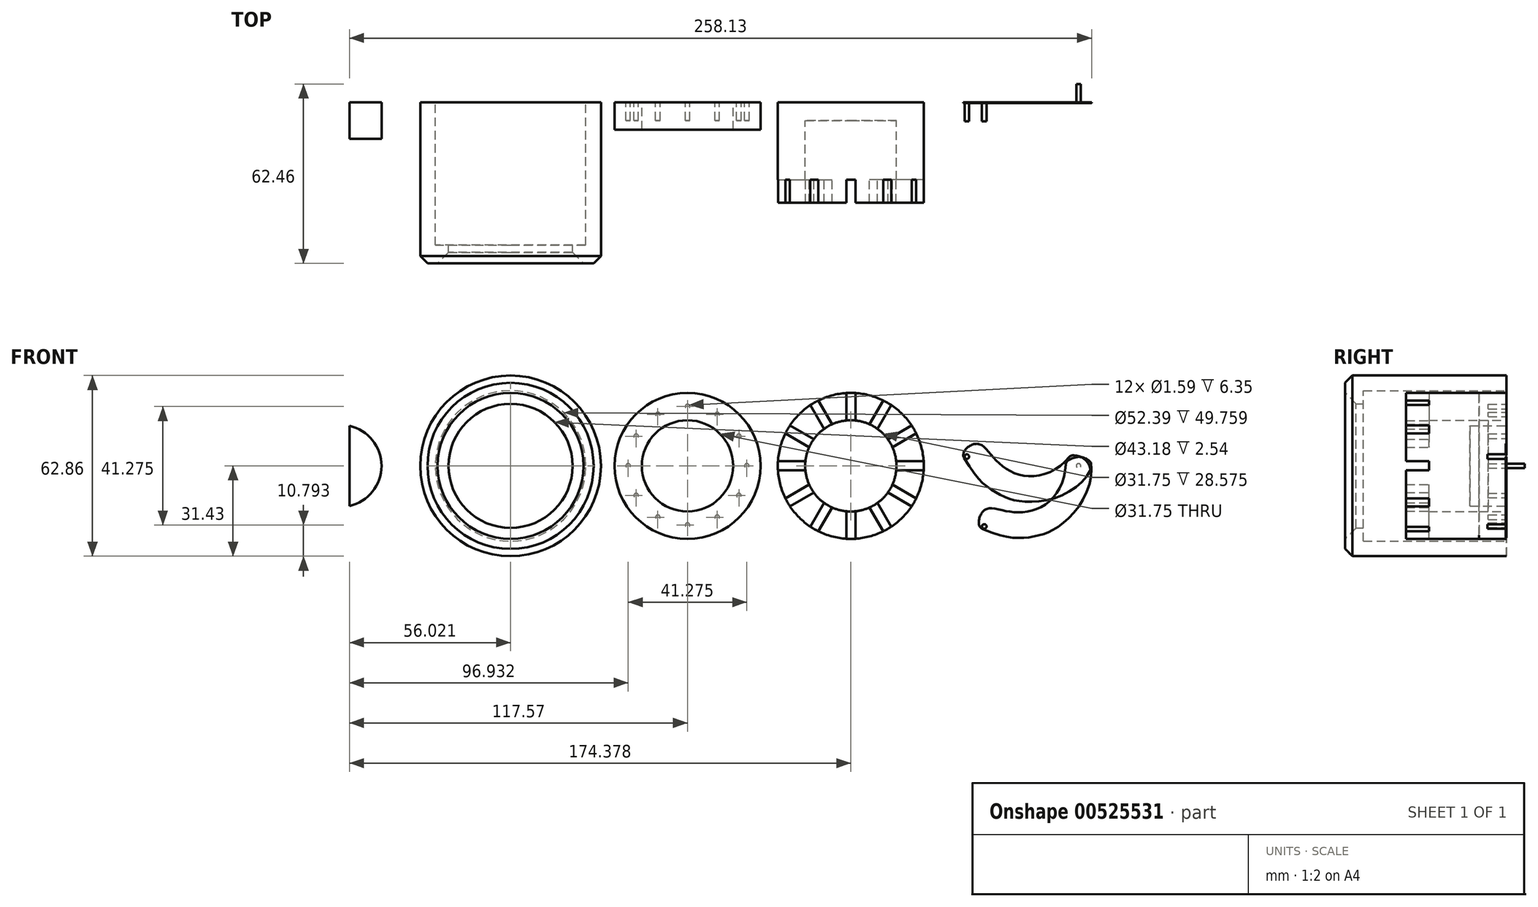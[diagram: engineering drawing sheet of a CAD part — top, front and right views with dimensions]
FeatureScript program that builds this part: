
annotation { "Feature Type Name" : "Feature", "Feature Type Description" : "" }
export const myFeature = defineFeature(function(context is Context, id is Id, definition is map)
    precondition{}
    {
        {
            var Q0;
            Q0=qCreatedBy(makeId("Front.planeOp"),FACE);
            var sketch = newSketch(context, id + "F0", { "sketchPlane" : qUnion([Q0])});
            skCircle(sketch, "E0", {"center": v(0, 0) * mm, "radius": 25.4 * mm});
            skCircle(sketch, "E1", {"center": v(0, 0) * mm, "radius": 15.88 * mm});
            skPoint(sketch, "E2", {"position": v(56.8, 0) * mm});
            skCircle(sketch, "E3", {"center": v(56.8, 0) * mm, "radius": 25.4 * mm});
            skCircle(sketch, "E4", {"center": v(56.8, 0) * mm, "radius": 15.88 * mm});
            skLineSegment(sketch, "E5", {"start": v(55.22, 25.35) * mm, "end": v(55.22, 15.8) * mm});
            skLineSegment(sketch, "E6", {"start": v(58.4, 25.35) * mm, "end": v(58.4, 15.8) * mm});
            skLineSegment(sketch, "E7", {"start": v(56.8, 0) * mm, "end": v(56.8, 25.4) * mm, "construction": true});
            skLineSegment(sketch, "E8", {"start": v(0, 0) * mm, "end": v(0, -25.4) * mm, "construction": true});
            skLineSegment(sketch, "E9", {"start": v(0, 0) * mm, "end": v(-25.4, 0) * mm, "construction": true});
            skLineSegment(sketch, "E10", {"start": v(0, 0) * mm, "end": v(-12.7, -22) * mm, "construction": true});
            skLineSegment(sketch, "E11", {"start": v(0, 0) * mm, "end": v(-22, -12.7) * mm, "construction": true});
            skCircle(sketch, "E12", {"center": v(0, 0) * mm, "radius": 20.64 * mm, "construction": true});
            skPoint(sketch, "E13.MirrorP", {"position": v(0, -20.64) * mm});
            skLineSegment(sketch, "E14", {"start": v(56.8, 0) * mm, "end": v(31.4, 0) * mm, "construction": true});
            skLineSegment(sketch, "E15", {"start": v(56.8, 0) * mm, "end": v(44.1, 22) * mm, "construction": true});
            skLineSegment(sketch, "E16", {"start": v(56.8, 0) * mm, "end": v(34.81, 12.7) * mm, "construction": true});
            skCircle(sketch, "E17", {"center": v(0, -20.64) * mm, "radius": 0.8 * mm});
            skPoint(sketch, "E18", {"position": v(115.4, 0) * mm});
            skCircle(sketch, "E19", {"center": v(115.4, 0) * mm, "radius": 15.88 * mm});
            skCircle(sketch, "E20", {"center": v(115.4, 0) * mm, "radius": 25.4 * mm});
            skLineSegment(sketch, "E21", {"start": v(115.4, 0) * mm, "end": v(140.8, 0) * mm, "construction": true});
            skLineSegment(sketch, "E22", {"start": v(115.4, 0) * mm, "end": v(115.4, -25.4) * mm, "construction": true});
            skLineSegment(sketch, "E23", {"start": v(115.4, 0) * mm, "end": v(137.4, -12.7) * mm, "construction": true});
            skLineSegment(sketch, "E24", {"start": v(115.4, 0) * mm, "end": v(128.1, -22) * mm, "construction": true});
            skLineSegment(sketch, "E25", {"start": v(115.4, 0) * mm, "end": v(102.7, -22) * mm, "construction": true});
            skCircle(sketch, "E26", {"center": v(115.4, 0) * mm, "radius": 20.64 * mm, "construction": true});
            skPoint(sketch, "E27", {"position": v(136.04, 0) * mm});
            skCircle(sketch, "E28", {"center": v(136.04, 0) * mm, "radius": 0.8 * mm});
            skPoint(sketch, "E29", {"position": v(103.23, -21.08) * mm});
            skCircle(sketch, "E30", {"center": v(103.23, -21.08) * mm, "radius": 0.8 * mm});
            skLineSegment(sketch, "E31", {"start": v(103.23, -21.08) * mm, "end": v(102.7, -22) * mm, "construction": true});
            skCircle(sketch, "E32.1.0", {"center": v(-10.32, -17.87) * mm, "radius": 0.8 * mm});
            skCircle(sketch, "E32.2.0", {"center": v(-17.87, -10.32) * mm, "radius": 0.8 * mm});
            skCircle(sketch, "E32.3.0", {"center": v(-20.64, 0) * mm, "radius": 0.8 * mm});
            skCircle(sketch, "E32.4.0", {"center": v(-17.87, 10.32) * mm, "radius": 0.8 * mm});
            skCircle(sketch, "E32.5.0", {"center": v(-10.32, 17.87) * mm, "radius": 0.8 * mm});
            skCircle(sketch, "E32.6.0", {"center": v(0, 20.64) * mm, "radius": 0.8 * mm});
            skCircle(sketch, "E32.7.0", {"center": v(10.32, 17.87) * mm, "radius": 0.8 * mm});
            skCircle(sketch, "E32.8.0", {"center": v(17.87, 10.32) * mm, "radius": 0.8 * mm});
            skCircle(sketch, "E32.9.0", {"center": v(20.64, 0) * mm, "radius": 0.8 * mm});
            skCircle(sketch, "E32.10.0", {"center": v(17.87, -10.32) * mm, "radius": 0.8 * mm});
            skCircle(sketch, "E32.11.0", {"center": v(10.32, -17.87) * mm, "radius": 0.8 * mm});
            skLineSegment(sketch, "E32.anchor1", {"start": v(0, 0) * mm, "end": v(0, -20.64) * mm, "construction": true});
            skLineSegment(sketch, "E32.anchor2", {"start": v(0, 0) * mm, "end": v(10.32, -17.87) * mm, "construction": true});
            skLineSegment(sketch, "E33.1.0", {"start": v(68.1, 22.75) * mm, "end": v(63.33, 14.47) * mm});
            skLineSegment(sketch, "E33.1.1", {"start": v(70.86, 21.16) * mm, "end": v(66.08, 12.89) * mm});
            skLineSegment(sketch, "E33.2.0", {"start": v(77.97, 14.05) * mm, "end": v(69.7, 9.27) * mm});
            skLineSegment(sketch, "E33.2.1", {"start": v(79.56, 11.3) * mm, "end": v(71.28, 6.52) * mm});
            skLineSegment(sketch, "E33.3.0", {"start": v(82.16, 1.59) * mm, "end": v(72.6, 1.59) * mm});
            skLineSegment(sketch, "E33.3.1", {"start": v(82.16, -1.59) * mm, "end": v(72.6, -1.59) * mm});
            skLineSegment(sketch, "E33.4.0", {"start": v(79.56, -11.3) * mm, "end": v(71.28, -6.52) * mm});
            skLineSegment(sketch, "E33.4.1", {"start": v(77.97, -14.05) * mm, "end": v(69.7, -9.27) * mm});
            skLineSegment(sketch, "E33.5.0", {"start": v(70.86, -21.16) * mm, "end": v(66.08, -12.89) * mm});
            skLineSegment(sketch, "E33.5.1", {"start": v(68.1, -22.75) * mm, "end": v(63.33, -14.47) * mm});
            skLineSegment(sketch, "E33.6.0", {"start": v(58.4, -25.35) * mm, "end": v(58.4, -15.8) * mm});
            skLineSegment(sketch, "E33.6.1", {"start": v(55.22, -25.35) * mm, "end": v(55.22, -15.8) * mm});
            skLineSegment(sketch, "E33.7.0", {"start": v(45.5, -22.75) * mm, "end": v(50.29, -14.47) * mm});
            skLineSegment(sketch, "E33.7.1", {"start": v(42.76, -21.16) * mm, "end": v(47.54, -12.89) * mm});
            skLineSegment(sketch, "E33.8.0", {"start": v(35.65, -14.05) * mm, "end": v(43.92, -9.27) * mm});
            skLineSegment(sketch, "E33.8.1", {"start": v(34.06, -11.3) * mm, "end": v(42.34, -6.52) * mm});
            skLineSegment(sketch, "E33.9.0", {"start": v(31.46, -1.59) * mm, "end": v(41.01, -1.59) * mm});
            skLineSegment(sketch, "E33.9.1", {"start": v(31.46, 1.59) * mm, "end": v(41.01, 1.59) * mm});
            skLineSegment(sketch, "E33.10.0", {"start": v(34.06, 11.3) * mm, "end": v(42.34, 6.52) * mm});
            skLineSegment(sketch, "E33.10.1", {"start": v(35.65, 14.05) * mm, "end": v(43.92, 9.27) * mm});
            skLineSegment(sketch, "E33.11.0", {"start": v(42.76, 21.16) * mm, "end": v(47.54, 12.89) * mm});
            skLineSegment(sketch, "E33.11.1", {"start": v(45.5, 22.75) * mm, "end": v(50.29, 14.47) * mm});
            skLineSegment(sketch, "E33.anchor1", {"start": v(56.8, 0) * mm, "end": v(55.22, 15.8) * mm, "construction": true});
            skLineSegment(sketch, "E33.anchor2", {"start": v(56.8, 0) * mm, "end": v(47.54, 12.89) * mm, "construction": true});
            skFitSpline(sketch, "E34", {"points": [v(104.11, -15.02) * mm, v(107.92, -15.1) * mm, v(115.4, -16.16) * mm, v(125.15, -12.93) * mm, v(131.55, 0.54) * mm], "startDerivative": vector(16.12, 9.46) * mm, "endDerivative": vector(0.3, 52.9) * mm});
            skFitSpline(sketch, "E35", {"points": [v(140.3, 1) * mm, v(137.15, -12.55) * mm, v(127.97, -21.77) * mm, v(121.95, -24.26) * mm, v(115.4, -25.08) * mm, v(102.7, -22) * mm], "startDerivative": vector(11.31, -46.24) * mm, "endDerivative": vector(-81.58, 33.81) * mm});
            skFitSpline(sketch, "E36", {"points": [v(140.3, 1) * mm, v(135.8, 3.1) * mm, v(131.55, 0.54) * mm], "startDerivative": vector(-1.34, 5.76) * mm, "endDerivative": vector(0.7, -5.07) * mm});
            skFitSpline(sketch, "E37", {"points": [v(104.11, -15.02) * mm, v(102.7, -22) * mm], "startDerivative": vector(-6.78, -1.61) * mm, "endDerivative": vector(8.29, -3.99) * mm});
            skPoint(sketch, "E38", {"position": v(-61.55, 0) * mm});
            skCircle(sketch, "E39", {"center": v(-61.55, 0) * mm, "radius": 25.4 * mm, "construction": true});
            skLineSegment(sketch, "E40", {"start": v(-61.55, 25.4) * mm, "end": v(-61.55, 26.2) * mm, "construction": true});
            skCircle(sketch, "E41", {"center": v(-61.55, 0) * mm, "radius": 26.2 * mm});
            skLineSegment(sketch, "E42", {"start": v(-61.55, 26.2) * mm, "end": v(-61.55, 31.43) * mm, "construction": true});
            skCircle(sketch, "E43", {"center": v(-61.55, 0) * mm, "radius": 31.43 * mm});
            skPoint(sketch, "E44", {"position": v(-120.75, 0) * mm});
            skCircle(sketch, "E45", {"center": v(-120.75, 0) * mm, "radius": 15.88 * mm, "construction": true});
            skLineSegment(sketch, "E46", {"start": v(-120.75, 14.29) * mm, "end": v(-120.75, 15.88) * mm, "construction": true});
            skCircle(sketch, "E47", {"center": v(-120.75, 0) * mm, "radius": 14.29 * mm});
            skLineSegment(sketch, "E48", {"start": v(-120.75, 14.29) * mm, "end": v(-120.75, -14.29) * mm, "construction": true});
            skLineSegment(sketch, "E49", {"start": v(-117.57, 13.93) * mm, "end": v(-117.57, -13.93) * mm});
            skLineSegment(sketch, "E50", {"start": v(-120.75, 0) * mm, "end": v(-117.57, 0) * mm, "construction": true});
            skCircle(sketch, "E51", {"center": v(-61.55, 0) * mm, "radius": 15.88 * mm, "construction": true});
            skLineSegment(sketch, "E52", {"start": v(-61.55, 25.4) * mm, "end": v(-61.55, 15.88) * mm, "construction": true});
            skCircle(sketch, "E53", {"center": v(-61.55, 0) * mm, "radius": 21.6 * mm});
            skLineSegment(sketch, "E54", {"start": v(-83.14, 0) * mm, "end": v(-86.95, 0) * mm, "construction": true});
            skSolve(sketch);
        }
        {
            var Q0;
            Q0=makeQuery(id+"F0.imprint","IMPRINT",FACE,{"disambiguationData":[TD([[makeQuery(id+"F0.imprint","IMPRINT",EDGE,{"derivedFrom":sQuery(id+"F0.wireOp",EDGE,"E0")}),1.0]])]});
            extrude(context, id + "F1", {"entities" : qUnion([Q0]), "depth" : 9.52 * mm, "offsetDistance" : 25.4 * mm});
        }
        {
            var Q0;
            Q0=makeQuery(id+"F0.imprint","IMPRINT",FACE,{"disambiguationData":[TD([[makeQuery(id+"F0.imprint","IMPRINT",EDGE,{"derivedFrom":sQuery(id+"F0.wireOp",EDGE,"s6iMMyBa-D8Xy-xpaJ-yUIR-B6XonEqi0sU5")}),1.0]])]});
            var Q1;
            Q1=makeQuery(id+"F0.imprint","IMPRINT",FACE,{"disambiguationData":[TD([[makeQuery(id+"F0.imprint","IMPRINT",EDGE,{"derivedFrom":sQuery(id+"F0.wireOp",EDGE,"E17")}),1.0]])]});
            var Q2;
            Q2=makeQuery(id+"F0.imprint","IMPRINT",FACE,{"disambiguationData":[TD([[makeQuery(id+"F0.imprint","IMPRINT",EDGE,{"derivedFrom":sQuery(id+"F0.wireOp",EDGE,"AtIlf3Au-Bq7Z-XsMa-0TNi-mlutI5QVi0Vg")}),1.0]])]});
            var Q3;
            Q3=makeQuery(id+"F0.imprint","IMPRINT",FACE,{"disambiguationData":[TD([[makeQuery(id+"F0.imprint","IMPRINT",EDGE,{"derivedFrom":sQuery(id+"F0.wireOp",EDGE,"LPBVN7vU-9lCU-ToEj-kHmf-HtTOnWTrnx0X")}),1.0]])]});
            var Q4;
            Q4=makeQuery(id+"F0.imprint","IMPRINT",FACE,{"disambiguationData":[TD([[makeQuery(id+"F0.imprint","IMPRINT",EDGE,{"derivedFrom":sQuery(id+"F0.wireOp",EDGE,"7G2NKrnm-SsA4-xEUf-SBrS-4CvmUcFiUhnw")}),1.0]])]});
            var Q5;
            Q5=makeQuery(id+"F0.imprint","IMPRINT",FACE,{"disambiguationData":[TD([[makeQuery(id+"F0.imprint","IMPRINT",EDGE,{"derivedFrom":sQuery(id+"F0.wireOp",EDGE,"5kcASDks-mq9c-bl9G-Ueh7-qEfE6t67Ye5v")}),1.0]])]});
            var Q6;
            Q6=makeQuery(id+"F0.imprint","IMPRINT",FACE,{"disambiguationData":[TD([[makeQuery(id+"F0.imprint","IMPRINT",EDGE,{"derivedFrom":sQuery(id+"F0.wireOp",EDGE,"E8oFIRYm-xzG7-Hb76-Ff9d-wAEOmmFZPbMu")}),1.0]])]});
            var Q7;
            Q7=makeQuery(id+"F0.imprint","IMPRINT",FACE,{"disambiguationData":[TD([[makeQuery(id+"F0.imprint","IMPRINT",EDGE,{"derivedFrom":sQuery(id+"F0.wireOp",EDGE,"81BxfGTd-YKAY-64cZ-fL0K-wmXlntmFN0K0")}),1.0]])]});
            var Q8;
            Q8=makeQuery(id+"F0.imprint","IMPRINT",FACE,{"disambiguationData":[TD([[makeQuery(id+"F0.imprint","IMPRINT",EDGE,{"derivedFrom":sQuery(id+"F0.wireOp",EDGE,"69LZ1IFe-H8bj-blPN-723C-wDsHpG4YcniU")}),1.0]])]});
            var Q9;
            Q9=makeQuery(id+"F0.imprint","IMPRINT",FACE,{"disambiguationData":[TD([[makeQuery(id+"F0.imprint","IMPRINT",EDGE,{"derivedFrom":sQuery(id+"F0.wireOp",EDGE,"Z80VmrJO-JPsI-7q49-229l-mwXOrK1fiucL")}),1.0]])]});
            var Q10;
            Q10=makeQuery(id+"F0.imprint","IMPRINT",FACE,{"disambiguationData":[TD([[makeQuery(id+"F0.imprint","IMPRINT",EDGE,{"derivedFrom":sQuery(id+"F0.wireOp",EDGE,"RLDDLLrd-eygd-P5LT-ErYo-oTRXF8rHV5MU")}),1.0]])]});
            var Q11;
            Q11=makeQuery(id+"F0.imprint","IMPRINT",FACE,{"disambiguationData":[TD([[makeQuery(id+"F0.imprint","IMPRINT",EDGE,{"derivedFrom":sQuery(id+"F0.wireOp",EDGE,"8nB9dmYy-pceP-ION0-gW85-PYhLIlr7NmiF")}),1.0]])]});
            var Q12;
            Q12=makeQuery(id+"F0.imprint","IMPRINT",FACE,{"disambiguationData":[TD([[makeQuery(id+"F0.imprint","IMPRINT",EDGE,{"derivedFrom":sQuery(id+"F0.wireOp",EDGE,"E32.1.0")}),1.0]])]});
            var Q13;
            Q13=makeQuery(id+"F0.imprint","IMPRINT",FACE,{"disambiguationData":[TD([[makeQuery(id+"F0.imprint","IMPRINT",EDGE,{"derivedFrom":sQuery(id+"F0.wireOp",EDGE,"E32.2.0")}),1.0]])]});
            var Q14;
            Q14=makeQuery(id+"F0.imprint","IMPRINT",FACE,{"disambiguationData":[TD([[makeQuery(id+"F0.imprint","IMPRINT",EDGE,{"derivedFrom":sQuery(id+"F0.wireOp",EDGE,"E32.3.0")}),1.0]])]});
            var Q15;
            Q15=makeQuery(id+"F0.imprint","IMPRINT",FACE,{"disambiguationData":[TD([[makeQuery(id+"F0.imprint","IMPRINT",EDGE,{"derivedFrom":sQuery(id+"F0.wireOp",EDGE,"E32.4.0")}),1.0]])]});
            var Q16;
            Q16=makeQuery(id+"F0.imprint","IMPRINT",FACE,{"disambiguationData":[TD([[makeQuery(id+"F0.imprint","IMPRINT",EDGE,{"derivedFrom":sQuery(id+"F0.wireOp",EDGE,"E32.8.0")}),1.0]])]});
            var Q17;
            Q17=makeQuery(id+"F0.imprint","IMPRINT",FACE,{"disambiguationData":[TD([[makeQuery(id+"F0.imprint","IMPRINT",EDGE,{"derivedFrom":sQuery(id+"F0.wireOp",EDGE,"E32.9.0")}),1.0]])]});
            var Q18;
            Q18=makeQuery(id+"F0.imprint","IMPRINT",FACE,{"disambiguationData":[TD([[makeQuery(id+"F0.imprint","IMPRINT",EDGE,{"derivedFrom":sQuery(id+"F0.wireOp",EDGE,"E32.10.0")}),1.0]])]});
            var Q19;
            Q19=makeQuery(id+"F0.imprint","IMPRINT",FACE,{"disambiguationData":[TD([[makeQuery(id+"F0.imprint","IMPRINT",EDGE,{"derivedFrom":sQuery(id+"F0.wireOp",EDGE,"E32.11.0")}),1.0]])]});
            var Q20;
            Q20=makeQuery(id+"F0.imprint","IMPRINT",FACE,{"disambiguationData":[TD([[makeQuery(id+"F0.imprint","IMPRINT",EDGE,{"derivedFrom":sQuery(id+"F0.wireOp",EDGE,"E32.5.0")}),1.0]])]});
            var Q21;
            Q21=makeQuery(id+"F0.imprint","IMPRINT",FACE,{"disambiguationData":[TD([[makeQuery(id+"F0.imprint","IMPRINT",EDGE,{"derivedFrom":sQuery(id+"F0.wireOp",EDGE,"E32.6.0")}),1.0]])]});
            var Q22;
            Q22=makeQuery(id+"F0.imprint","IMPRINT",FACE,{"disambiguationData":[TD([[makeQuery(id+"F0.imprint","IMPRINT",EDGE,{"derivedFrom":sQuery(id+"F0.wireOp",EDGE,"E32.7.0")}),1.0]])]});
            extrude(context, id + "F2", {"entities" : qUnion([Q0, Q1, Q2, Q3, Q4, Q5, Q6, Q7, Q8, Q9, Q10, Q11, Q12, Q13, Q14, Q15, Q16, Q17, Q18, Q19, Q20, Q21, Q22]), "operationType" : NewBodyOperationType.ADD, "depth" : 9.52 * mm, "offsetDistance" : 25.4 * mm, "hasSecondDirection" : true, "secondDirectionOppositeDirection" : false, "secondDirectionDepth" : 6.35 * mm});
        }
        {
            var Q0;
            {var subQ0=sQuery(id+"F0.wireOp",EDGE,"E5");Q0=makeQuery(id+"F0.imprint","IMPRINT",FACE,{"disambiguationData":[TD([[makeQuery(id+"F0.imprint","IMPRINT",EDGE,{"derivedFrom":subQ0}),-1.0]])]});}
            var Q1;
            {var subQ0=sQuery(id+"F0.wireOp",EDGE,"E6");Q1=makeQuery(id+"F0.imprint","IMPRINT",FACE,{"disambiguationData":[TD([[makeQuery(id+"F0.imprint","IMPRINT",EDGE,{"derivedFrom":subQ0}),1.0]])]});}
            var Q2;
            {var subQ0=sQuery(id+"F0.wireOp",EDGE,"fbf749ff-cb35-4a6c-9a33-f2034c6c4bd01.MirrorCS");Q2=makeQuery(id+"F0.imprint","IMPRINT",FACE,{"disambiguationData":[TD([[makeQuery(id+"F0.imprint","IMPRINT",EDGE,{"derivedFrom":subQ0}),-1.0]])]});}
            var Q3;
            {var subQ0=sQuery(id+"F0.wireOp",EDGE,"2fd75d67-c833-453d-aed9-928d4629f6e80.MirrorCS");Q3=makeQuery(id+"F0.imprint","IMPRINT",FACE,{"disambiguationData":[TD([[makeQuery(id+"F0.imprint","IMPRINT",EDGE,{"derivedFrom":subQ0}),1.0]])]});}
            var Q4;
            {var subQ0=sQuery(id+"F0.wireOp",EDGE,"2fd75d67-c833-453d-aed9-928d4629f6e81.MirrorCS");Q4=makeQuery(id+"F0.imprint","IMPRINT",FACE,{"disambiguationData":[TD([[makeQuery(id+"F0.imprint","IMPRINT",EDGE,{"derivedFrom":subQ0}),-1.0]])]});}
            var Q5;
            {var subQ0=sQuery(id+"F0.wireOp",EDGE,"f250c77a-9c41-4284-acdc-d1beea1743cd4.MirrorCS");Q5=makeQuery(id+"F0.imprint","IMPRINT",FACE,{"disambiguationData":[TD([[makeQuery(id+"F0.imprint","IMPRINT",EDGE,{"derivedFrom":subQ0}),-1.0]])]});}
            var Q6;
            {var subQ0=sQuery(id+"F0.wireOp",EDGE,"0f70c7a6-16d2-4b7e-8e74-36adbd6650231.MirrorCS");Q6=makeQuery(id+"F0.imprint","IMPRINT",FACE,{"disambiguationData":[TD([[makeQuery(id+"F0.imprint","IMPRINT",EDGE,{"derivedFrom":subQ0}),-1.0]])]});}
            var Q7;
            {var subQ0=sQuery(id+"F0.wireOp",EDGE,"0f70c7a6-16d2-4b7e-8e74-36adbd6650230.MirrorCS");Q7=makeQuery(id+"F0.imprint","IMPRINT",FACE,{"disambiguationData":[TD([[makeQuery(id+"F0.imprint","IMPRINT",EDGE,{"derivedFrom":subQ0}),1.0]])]});}
            var Q8;
            {var subQ0=sQuery(id+"F0.wireOp",EDGE,"f250c77a-9c41-4284-acdc-d1beea1743cd1.MirrorCS");Q8=makeQuery(id+"F0.imprint","IMPRINT",FACE,{"disambiguationData":[TD([[makeQuery(id+"F0.imprint","IMPRINT",EDGE,{"derivedFrom":subQ0}),1.0]])]});}
            var Q9;
            {var subQ0=sQuery(id+"F0.wireOp",EDGE,"9w2d8wIe-WXym-CVrp-cu3j-IBF0zttnJeDN");Q9=makeQuery(id+"F0.imprint","IMPRINT",FACE,{"disambiguationData":[TD([[makeQuery(id+"F0.imprint","IMPRINT",EDGE,{"derivedFrom":subQ0}),1.0]])]});}
            var Q10;
            {var subQ0=sQuery(id+"F0.wireOp",EDGE,"rNfeRRnT-j6xk-gXZh-7wYH-FjU2ABQCOJYs");Q10=makeQuery(id+"F0.imprint","IMPRINT",FACE,{"disambiguationData":[TD([[makeQuery(id+"F0.imprint","IMPRINT",EDGE,{"derivedFrom":subQ0}),-1.0]])]});}
            var Q11;
            {var subQ0=sQuery(id+"F0.wireOp",EDGE,"0O4XiFiV-CEn2-lq8x-aV4j-AC8LqMBIBljq");Q11=makeQuery(id+"F0.imprint","IMPRINT",FACE,{"disambiguationData":[TD([[makeQuery(id+"F0.imprint","IMPRINT",EDGE,{"derivedFrom":subQ0}),-1.0]])]});}
            var Q12;
            {var subQ0=sQuery(id+"F0.wireOp",EDGE,"E33.1.1");Q12=makeQuery(id+"F0.imprint","IMPRINT",FACE,{"disambiguationData":[TD([[makeQuery(id+"F0.imprint","IMPRINT",EDGE,{"derivedFrom":subQ0}),1.0]])]});}
            var Q13;
            {var subQ0=sQuery(id+"F0.wireOp",EDGE,"E33.10.1");Q13=makeQuery(id+"F0.imprint","IMPRINT",FACE,{"disambiguationData":[TD([[makeQuery(id+"F0.imprint","IMPRINT",EDGE,{"derivedFrom":subQ0}),1.0]])]});}
            var Q14;
            {var subQ0=sQuery(id+"F0.wireOp",EDGE,"E33.9.1");Q14=makeQuery(id+"F0.imprint","IMPRINT",FACE,{"disambiguationData":[TD([[makeQuery(id+"F0.imprint","IMPRINT",EDGE,{"derivedFrom":subQ0}),1.0]])]});}
            var Q15;
            {var subQ0=sQuery(id+"F0.wireOp",EDGE,"E33.8.1");Q15=makeQuery(id+"F0.imprint","IMPRINT",FACE,{"disambiguationData":[TD([[makeQuery(id+"F0.imprint","IMPRINT",EDGE,{"derivedFrom":subQ0}),1.0]])]});}
            var Q16;
            {var subQ0=sQuery(id+"F0.wireOp",EDGE,"E33.7.1");Q16=makeQuery(id+"F0.imprint","IMPRINT",FACE,{"disambiguationData":[TD([[makeQuery(id+"F0.imprint","IMPRINT",EDGE,{"derivedFrom":subQ0}),1.0]])]});}
            var Q17;
            {var subQ0=sQuery(id+"F0.wireOp",EDGE,"E33.6.1");Q17=makeQuery(id+"F0.imprint","IMPRINT",FACE,{"disambiguationData":[TD([[makeQuery(id+"F0.imprint","IMPRINT",EDGE,{"derivedFrom":subQ0}),1.0]])]});}
            var Q18;
            {var subQ0=sQuery(id+"F0.wireOp",EDGE,"E33.5.1");Q18=makeQuery(id+"F0.imprint","IMPRINT",FACE,{"disambiguationData":[TD([[makeQuery(id+"F0.imprint","IMPRINT",EDGE,{"derivedFrom":subQ0}),1.0]])]});}
            var Q19;
            {var subQ0=sQuery(id+"F0.wireOp",EDGE,"E33.4.1");Q19=makeQuery(id+"F0.imprint","IMPRINT",FACE,{"disambiguationData":[TD([[makeQuery(id+"F0.imprint","IMPRINT",EDGE,{"derivedFrom":subQ0}),1.0]])]});}
            var Q20;
            {var subQ0=sQuery(id+"F0.wireOp",EDGE,"E33.3.1");Q20=makeQuery(id+"F0.imprint","IMPRINT",FACE,{"disambiguationData":[TD([[makeQuery(id+"F0.imprint","IMPRINT",EDGE,{"derivedFrom":subQ0}),1.0]])]});}
            var Q21;
            {var subQ0=sQuery(id+"F0.wireOp",EDGE,"E33.2.1");Q21=makeQuery(id+"F0.imprint","IMPRINT",FACE,{"disambiguationData":[TD([[makeQuery(id+"F0.imprint","IMPRINT",EDGE,{"derivedFrom":subQ0}),1.0]])]});}
            extrude(context, id + "F3", {"entities" : qUnion([Q0, Q1, Q2, Q3, Q4, Q5, Q6, Q7, Q8, Q9, Q10, Q11, Q12, Q13, Q14, Q15, Q16, Q17, Q18, Q19, Q20, Q21]), "depth" : 34.92 * mm, "offsetDistance" : 25.4 * mm});
        }
        {
            var Q0;
            {var subQ0=sQuery(id+"F0.wireOp",EDGE,"ZaU0kOoB-QJxD-Patt-xqo6-pcWAK5y8749o");Q0=makeQuery(id+"F0.imprint","IMPRINT",FACE,{"disambiguationData":[TD([[makeQuery(id+"F0.imprint","IMPRINT",EDGE,{"derivedFrom":subQ0}),1.0]])]});}
            var Q1;
            {var subQ0=sQuery(id+"F0.wireOp",EDGE,"wwbT7rCj-GxeO-RORG-loiN-BMqO9dk52bbs");Q1=makeQuery(id+"F0.imprint","IMPRINT",FACE,{"disambiguationData":[TD([[makeQuery(id+"F0.imprint","IMPRINT",EDGE,{"derivedFrom":subQ0}),1.0]])]});}
            var Q2;
            {var subQ0=sQuery(id+"F0.wireOp",EDGE,"rNfeRRnT-j6xk-gXZh-7wYH-FjU2ABQCOJYs");Q2=makeQuery(id+"F0.imprint","IMPRINT",FACE,{"disambiguationData":[TD([[makeQuery(id+"F0.imprint","IMPRINT",EDGE,{"derivedFrom":subQ0}),1.0]])]});}
            var Q3;
            {var subQ0=sQuery(id+"F0.wireOp",EDGE,"f250c77a-9c41-4284-acdc-d1beea1743cd0.MirrorCS");Q3=makeQuery(id+"F0.imprint","IMPRINT",FACE,{"disambiguationData":[TD([[makeQuery(id+"F0.imprint","IMPRINT",EDGE,{"derivedFrom":subQ0}),-1.0]])]});}
            var Q4;
            {var subQ0=sQuery(id+"F0.wireOp",EDGE,"f250c77a-9c41-4284-acdc-d1beea1743cd2.MirrorCS");Q4=makeQuery(id+"F0.imprint","IMPRINT",FACE,{"disambiguationData":[TD([[makeQuery(id+"F0.imprint","IMPRINT",EDGE,{"derivedFrom":subQ0}),1.0]])]});}
            var Q5;
            {var subQ0=sQuery(id+"F0.wireOp",EDGE,"0f70c7a6-16d2-4b7e-8e74-36adbd6650230.MirrorCS");Q5=makeQuery(id+"F0.imprint","IMPRINT",FACE,{"disambiguationData":[TD([[makeQuery(id+"F0.imprint","IMPRINT",EDGE,{"derivedFrom":subQ0}),-1.0]])]});}
            var Q6;
            {var subQ0=sQuery(id+"F0.wireOp",EDGE,"f250c77a-9c41-4284-acdc-d1beea1743cd5.MirrorCS");Q6=makeQuery(id+"F0.imprint","IMPRINT",FACE,{"disambiguationData":[TD([[makeQuery(id+"F0.imprint","IMPRINT",EDGE,{"derivedFrom":subQ0}),1.0]])]});}
            var Q7;
            {var subQ0=sQuery(id+"F0.wireOp",EDGE,"f250c77a-9c41-4284-acdc-d1beea1743cd4.MirrorCS");Q7=makeQuery(id+"F0.imprint","IMPRINT",FACE,{"disambiguationData":[TD([[makeQuery(id+"F0.imprint","IMPRINT",EDGE,{"derivedFrom":subQ0}),1.0]])]});}
            var Q8;
            {var subQ0=sQuery(id+"F0.wireOp",EDGE,"2fd75d67-c833-453d-aed9-928d4629f6e80.MirrorCS");Q8=makeQuery(id+"F0.imprint","IMPRINT",FACE,{"disambiguationData":[TD([[makeQuery(id+"F0.imprint","IMPRINT",EDGE,{"derivedFrom":subQ0}),-1.0]])]});}
            var Q9;
            {var subQ0=sQuery(id+"F0.wireOp",EDGE,"fbf749ff-cb35-4a6c-9a33-f2034c6c4bd02.MirrorCS");Q9=makeQuery(id+"F0.imprint","IMPRINT",FACE,{"disambiguationData":[TD([[makeQuery(id+"F0.imprint","IMPRINT",EDGE,{"derivedFrom":subQ0}),-1.0]])]});}
            var Q10;
            {var subQ0=sQuery(id+"F0.wireOp",EDGE,"fbf749ff-cb35-4a6c-9a33-f2034c6c4bd00.MirrorCS");Q10=makeQuery(id+"F0.imprint","IMPRINT",FACE,{"disambiguationData":[TD([[makeQuery(id+"F0.imprint","IMPRINT",EDGE,{"derivedFrom":subQ0}),-1.0]])]});}
            var Q11;
            {var subQ0=sQuery(id+"F0.wireOp",EDGE,"E5");Q11=makeQuery(id+"F0.imprint","IMPRINT",FACE,{"disambiguationData":[TD([[makeQuery(id+"F0.imprint","IMPRINT",EDGE,{"derivedFrom":subQ0}),1.0]])]});}
            var Q12;
            {var subQ0=sQuery(id+"F0.wireOp",EDGE,"E33.1.0");Q12=makeQuery(id+"F0.imprint","IMPRINT",FACE,{"disambiguationData":[TD([[makeQuery(id+"F0.imprint","IMPRINT",EDGE,{"derivedFrom":subQ0}),1.0]])]});}
            var Q13;
            {var subQ0=sQuery(id+"F0.wireOp",EDGE,"E33.2.0");Q13=makeQuery(id+"F0.imprint","IMPRINT",FACE,{"disambiguationData":[TD([[makeQuery(id+"F0.imprint","IMPRINT",EDGE,{"derivedFrom":subQ0}),1.0]])]});}
            var Q14;
            {var subQ0=sQuery(id+"F0.wireOp",EDGE,"E33.3.0");Q14=makeQuery(id+"F0.imprint","IMPRINT",FACE,{"disambiguationData":[TD([[makeQuery(id+"F0.imprint","IMPRINT",EDGE,{"derivedFrom":subQ0}),1.0]])]});}
            var Q15;
            {var subQ0=sQuery(id+"F0.wireOp",EDGE,"E33.10.0");Q15=makeQuery(id+"F0.imprint","IMPRINT",FACE,{"disambiguationData":[TD([[makeQuery(id+"F0.imprint","IMPRINT",EDGE,{"derivedFrom":subQ0}),1.0]])]});}
            var Q16;
            {var subQ0=sQuery(id+"F0.wireOp",EDGE,"E33.11.0");Q16=makeQuery(id+"F0.imprint","IMPRINT",FACE,{"disambiguationData":[TD([[makeQuery(id+"F0.imprint","IMPRINT",EDGE,{"derivedFrom":subQ0}),1.0]])]});}
            var Q17;
            {var subQ0=sQuery(id+"F0.wireOp",EDGE,"E33.9.0");Q17=makeQuery(id+"F0.imprint","IMPRINT",FACE,{"disambiguationData":[TD([[makeQuery(id+"F0.imprint","IMPRINT",EDGE,{"derivedFrom":subQ0}),1.0]])]});}
            var Q18;
            {var subQ0=sQuery(id+"F0.wireOp",EDGE,"E33.4.0");Q18=makeQuery(id+"F0.imprint","IMPRINT",FACE,{"disambiguationData":[TD([[makeQuery(id+"F0.imprint","IMPRINT",EDGE,{"derivedFrom":subQ0}),1.0]])]});}
            var Q19;
            {var subQ0=sQuery(id+"F0.wireOp",EDGE,"E33.8.0");Q19=makeQuery(id+"F0.imprint","IMPRINT",FACE,{"disambiguationData":[TD([[makeQuery(id+"F0.imprint","IMPRINT",EDGE,{"derivedFrom":subQ0}),1.0]])]});}
            var Q20;
            {var subQ0=sQuery(id+"F0.wireOp",EDGE,"E33.7.0");Q20=makeQuery(id+"F0.imprint","IMPRINT",FACE,{"disambiguationData":[TD([[makeQuery(id+"F0.imprint","IMPRINT",EDGE,{"derivedFrom":subQ0}),1.0]])]});}
            var Q21;
            {var subQ0=sQuery(id+"F0.wireOp",EDGE,"E33.6.0");Q21=makeQuery(id+"F0.imprint","IMPRINT",FACE,{"disambiguationData":[TD([[makeQuery(id+"F0.imprint","IMPRINT",EDGE,{"derivedFrom":subQ0}),1.0]])]});}
            var Q22;
            {var subQ0=sQuery(id+"F0.wireOp",EDGE,"E33.5.0");Q22=makeQuery(id+"F0.imprint","IMPRINT",FACE,{"disambiguationData":[TD([[makeQuery(id+"F0.imprint","IMPRINT",EDGE,{"derivedFrom":subQ0}),1.0]])]});}
            extrude(context, id + "F4", {"entities" : qUnion([Q0, Q1, Q2, Q3, Q4, Q5, Q6, Q7, Q8, Q9, Q10, Q11, Q12, Q13, Q14, Q15, Q16, Q17, Q18, Q19, Q20, Q21, Q22]), "operationType" : NewBodyOperationType.ADD, "depth" : 26.99 * mm, "offsetDistance" : 25.4 * mm});
        }
        {
            var Q0;
            {var subQ0=sQuery(id+"F0.wireOp",EDGE,"E4");var subQ18=makeQuery(id+"F0.imprint","INTERSECT",VERTEX,{"derivedFrom":[subQ0,sQuery(id+"F0.wireOp",EDGE,"2fd75d67-c833-453d-aed9-928d4629f6e80.MirrorCS")]});Q0=makeQuery(id+"F0.imprint","IMPRINT",FACE,{"disambiguationData":[TD([[makeQuery(id+"F0.imprint","IMPRINT",EDGE,{"disambiguationData":[TD([[subQ18,-1.0]])],"derivedFrom":subQ0}),1.0]])]});}
            extrude(context, id + "F5", {"entities" : qUnion([Q0]), "operationType" : NewBodyOperationType.ADD, "depth" : 6.35 * mm, "offsetDistance" : 25.4 * mm});
        }
        {
            var Q0;
            Q0=makeQuery(id+"F0.imprint","IMPRINT",FACE,{"disambiguationData":[TD([[makeQuery(id+"F0.imprint","IMPRINT",EDGE,{"derivedFrom":sQuery(id+"F0.wireOp",EDGE,"E28")}),-1.0]])]});
            extrude(context, id + "F6", {"entities" : qUnion([Q0]), "depth" : 0.27 * mm, "offsetDistance" : 25.4 * mm});
        }
        {
            var Q0;
            Q0=makeQuery(id+"F0.imprint","IMPRINT",FACE,{"disambiguationData":[TD([[makeQuery(id+"F0.imprint","IMPRINT",EDGE,{"derivedFrom":sQuery(id+"F0.wireOp",EDGE,"E28")}),1.0]])]});
            extrude(context, id + "F7", {"entities" : qUnion([Q0]), "operationType" : NewBodyOperationType.ADD, "oppositeDirection" : true, "depth" : 6.35 * mm, "offsetDistance" : 25.4 * mm, "hasSecondDirection" : true, "secondDirectionOppositeDirection" : false, "secondDirectionDepth" : 0.27 * mm});
        }
        {
            var Q0;
            Q0=makeQuery(id+"F0.imprint","IMPRINT",FACE,{"disambiguationData":[TD([[makeQuery(id+"F0.imprint","IMPRINT",EDGE,{"derivedFrom":sQuery(id+"F0.wireOp",EDGE,"E30")}),1.0]])]});
            var Q1;
            Q1=sQuery(id+"F0.wireOp",EDGE,"E30");
            extrude(context, id + "F8", {"entities" : qUnion([Q0]), "operationType" : NewBodyOperationType.ADD, "surfaceEntities" : qUnion([Q1]), "depth" : 6.62 * mm, "offsetDistance" : 25.4 * mm});
        }
        {
            var Q0;
            Q0=makeQuery(id+"F6.opExtrude","SWEPT_BODY",BODY,{"disambiguationData":[OSD([sQuery(id+"F0.wireOp",EDGE,"E19"),sQuery(id+"F0.wireOp",EDGE,"E20"),sQuery(id+"F0.wireOp",EDGE,"E28"),sQuery(id+"F0.wireOp",EDGE,"E30"),sQuery(id+"F0.wireOp",EDGE,"9cQofrjR-p9AV-AqL5-6mUo-xMYrZhE80EzS"),sQuery(id+"F0.wireOp",EDGE,"MxygyAQR-i0tx-qIU0-I9ef-YA1Th21NrxdS")])]});
            var Q1;
            Q1=makeQuery(id+"F7.opExtrude","SWEPT_FACE",FACE,{"disambiguationData":[OSD([sQuery(id+"F0.wireOp",EDGE,"E28")])]});
            transform(context, id + "F9", {"entities" : qUnion([Q0]), "transformType" : TransformType.ROTATION, "transformAxis" : qUnion([Q1]), "angle" : 37.47 * degree, "oppositeDirection" : true, "makeCopy" : true});
        }
        {
            var Q0;
            Q0=makeQuery(id+"F0.imprint","IMPRINT",FACE,{"disambiguationData":[TD([[makeQuery(id+"F0.imprint","IMPRINT",EDGE,{"derivedFrom":sQuery(id+"F0.wireOp",EDGE,"E41")}),-1.0]])]});
            extrude(context, id + "F10", {"entities" : qUnion([Q0]), "depth" : 49.76 * mm, "offsetDistance" : 25.4 * mm});
        }
        {
            var Q0;
            Q0=makeQuery(id+"F10.opExtrude","CAP_FACE",FACE,{"disambiguationData":[OSD([sQuery(id+"F0.wireOp",EDGE,"E41"),sQuery(id+"F0.wireOp",EDGE,"E43")])],"isStart":false});
            extrude(context, id + "F11", {"entities" : qUnion([Q0]), "operationType" : NewBodyOperationType.ADD, "surfaceOperationType" : NewSurfaceOperationType.ADD, "depth" : 6.35 * mm, "offsetDistance" : 25.4 * mm, "hasSecondDirection" : true, "secondDirectionOppositeDirection" : true, "secondDirectionDepth" : 49.76 * mm});
        }
        {
            var Q0;
            Q0=makeQuery(id+"F0.imprint","IMPRINT",FACE,{"disambiguationData":[TD([[makeQuery(id+"F0.imprint","IMPRINT",EDGE,{"derivedFrom":sQuery(id+"F0.wireOp",EDGE,"E41")}),1.0]])]});
            extrude(context, id + "F12", {"entities" : qUnion([Q0]), "operationType" : NewBodyOperationType.ADD, "surfaceOperationType" : NewSurfaceOperationType.ADD, "depth" : 56.1 * mm, "offsetDistance" : 25.4 * mm, "hasSecondDirection" : true, "secondDirectionOppositeDirection" : false, "secondDirectionDepth" : 49.76 * mm});
        }
        {
            var Q0;
            Q0=makeQuery(id+"F12.opExtrude","CAP_EDGE",EDGE,{"disambiguationData":[OSD([sQuery(id+"F0.wireOp",EDGE,"E53")])],"isStart":false});
            chamfer(context, id + "F13", {"entities" : qUnion([Q0]), "width" : 3.8 * mm, "tangentPropagation" : true});
        }
        {
            var Q0;
            Q0=makeQuery(id+"F11.opExtrude","CAP_EDGE",EDGE,{"disambiguationData":[OSD([sQuery(id+"F0.wireOp",EDGE,"E43")])],"isStart":false});
            chamfer(context, id + "F14", {"entities" : qUnion([Q0]), "width" : 2.54 * mm, "tangentPropagation" : true});
        }
        {
            var Q0;
            {var subQ0=sQuery(id+"F0.wireOp",EDGE,"E49");Q0=makeQuery(id+"F0.imprint","IMPRINT",FACE,{"disambiguationData":[TD([[makeQuery(id+"F0.imprint","IMPRINT",EDGE,{"derivedFrom":subQ0}),1.0]])]});}
            extrude(context, id + "F15", {"entities" : qUnion([Q0]), "depth" : 12.7 * mm, "offsetDistance" : 25.4 * mm});
        }
    });
